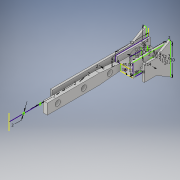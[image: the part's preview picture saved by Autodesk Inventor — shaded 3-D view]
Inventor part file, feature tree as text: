
AUTODESK INVENTOR PART (.ipt)
format: ipt  version: 2019 (Build 230136000, 136)  size: 475,136 bytes
history: native  units: in
note: dims shown in document units (in); Inventor stores cm internally (conversion verified against a paired STEP export)
features: extrude x23, sketch x20
ambient origin geometry x8: Origin, YZ Plane, XZ Plane, XY Plane, X Axis, Y Axis, Z Axis, Center Point
bodies: Solid1 (feature_tree)
feature tree (43):
  sketch  "Sketch1"  dims[d3=0.3346in d4=0.0394in]
  extrude  "Extrusion1"  Depth=0.0394in
  extrude  "Extrusion2"  Depth=0.0787in
  extrude  "Extrusion3"  Depth=0.0394in
  extrude  "Extrusion4"  Depth=0.0787in
  sketch  "Sketch3"  dims[d7=0.0787in d8=0.0394in]
  sketch  "Sketch4"  dims[d9=0.0394in d10=0.0787in]
  extrude  "Extrusion5"  Depth=0.0787in
  sketch  "Sketch5"  dims[d11=0.0787in d12=0.0787in]
  extrude  "Extrusion6"  Depth=0.0787in
  extrude  "Extrusion7"  Depth=0.0787in
  sketch  "Sketch7"  dims[d15=0.0787in d16=0.0787in]
  extrude  "Extrusion8"  Depth=0.9843in TaperAngle=0.0deg
  extrude  "Extrusion9"  Depth=0.2362in TaperAngle=0.0deg
  sketch  "Sketch10"  dims[d17=0.0787in d18=0.9843in d19=0.0in]
  extrude  "Extrusion12"  Depth=0.0787in TaperAngle=0.0deg
  extrude  "Extrusion13"  Depth=0.4724in
  sketch  "Sketch11"  dims[d20=0.1181in d21=0.0in d22=0.2362in d23=0.0in]
  extrude  "Extrusion14"  TaperAngle=45.0deg  [1 undecoded]
  sketch  "Sketch13"  dims[d28=0.1181in d29=0.0in d30=0.4724in]
  extrude  "Extrusion21"  Depth=0.4724in
  extrude  "Extrusion22"  TaperAngle=45.0deg  [1 undecoded]
  extrude  "Extrusion23"  Depth=0.0787in
  extrude  "Extrusion24"  Depth=0.3937in TaperAngle=0.0deg
  extrude  "Extrusion25"  Depth=0.0787in
  extrude  "Extrusion26"  Depth=0.0787in
  sketch  "Sketch24"  dims[d63=0.2362in d64=0.0787in]
  extrude  "Extrusion27"  Depth=0.0787in
  extrude  "Extrusion28"  Depth=0.0787in
  sketch  "Sketch25"  dims[d65=0.2362in d66=0.0787in]
  extrude  "Extrusion29"  Depth=0.0787in
  extrude  "Extrusion30"  Depth=0.9843in TaperAngle=0.0deg
  extrude  "Extrusion31"  Depth=0.0787in TaperAngle=0.0deg
  sketch  "Sketch2"  dims[d5=0.6693in d6=0.0787in]
  sketch  "Sketch6"  dims[d13=0.0787in d14=0.0787in]
  sketch  "Sketch12"  dims[d25=0.0512in d26=0.0787in d27=0.0in]
  sketch  "Sketch18"  dims[d31=45.0deg d32=45.0deg]
  sketch  "Sketch19"  dims[d33=0.0787in d34=0.0in d35=0.4724in]
  sketch  "Sketch20"  dims[d36=90.0deg d37=45.0deg]
  sketch  "Sketch21"  dims[d38=0.0787in d39=0.0in d40=0.0709in]
  sketch  "Sketch22"  dims[d41=0.1575in d42=0.3937in d43=0.0in]
  sketch  "Sketch23"  dims[d44=2.3622in d45=0.0in d62=0.0787in]
  sketch  "Sketch26"  dims[d67=1.1811in d68=0.0787in d69=1.1811in d70=0.9843in d71=0.0in d72=5.1181in d73=0.0in d74=30.0deg d75=30.0deg d76=5.1181in d77=0.0in d79=0.0787in d80=0.0787in d81=0.0787in d82=0.0787in d83=0.0787in d106=1.9685in d107=0.3937in d108=0.1575in d109=0.0in d110=0.1575in d111=0.0in d112=0.1969in d113=0.9843in d114=0.1969in d115=0.9843in d116=0.1969in d117=0.1575in d118=0.0in d131=0.0787in d132=0.0787in d133=0.0787in d134=0.0787in d135=0.0787in d136=0.0787in d137=0.0787in d138=0.0787in d139=0.0787in d140=0.0787in d141=0.0787in d142=0.0787in d143=0.0787in d144=0.0787in d145=0.0787in d146=0.0787in d147=0.0787in d148=0.0in d149=0.0787in d150=0.0787in d151=0.0787in d152=0.0787in d153=0.0787in d154=0.0787in d155=0.0787in d156=0.0787in d157=0.0787in d158=0.0in d159=1.5748in d160=0.5906in d161=0.1969in d162=0.0in d163=1.2598in d164=0.315in d165=0.5906in d166=0.0787in d167=0.0in d168=0.0787in d169=0.0in d170=1.2598in d171=0.4331in d172=0.5512in d173=0.0787in d174=0.0in d175=0.0787in d176=0.0in d177=0.7087in d178=0.3937in d179=0.0787in d180=0.0in]
note: 2 required parameter values undecoded (feature->parameter linkage not recoverable at this tier; creation-order binding heuristic only, values carry confidence <= 0.55)
